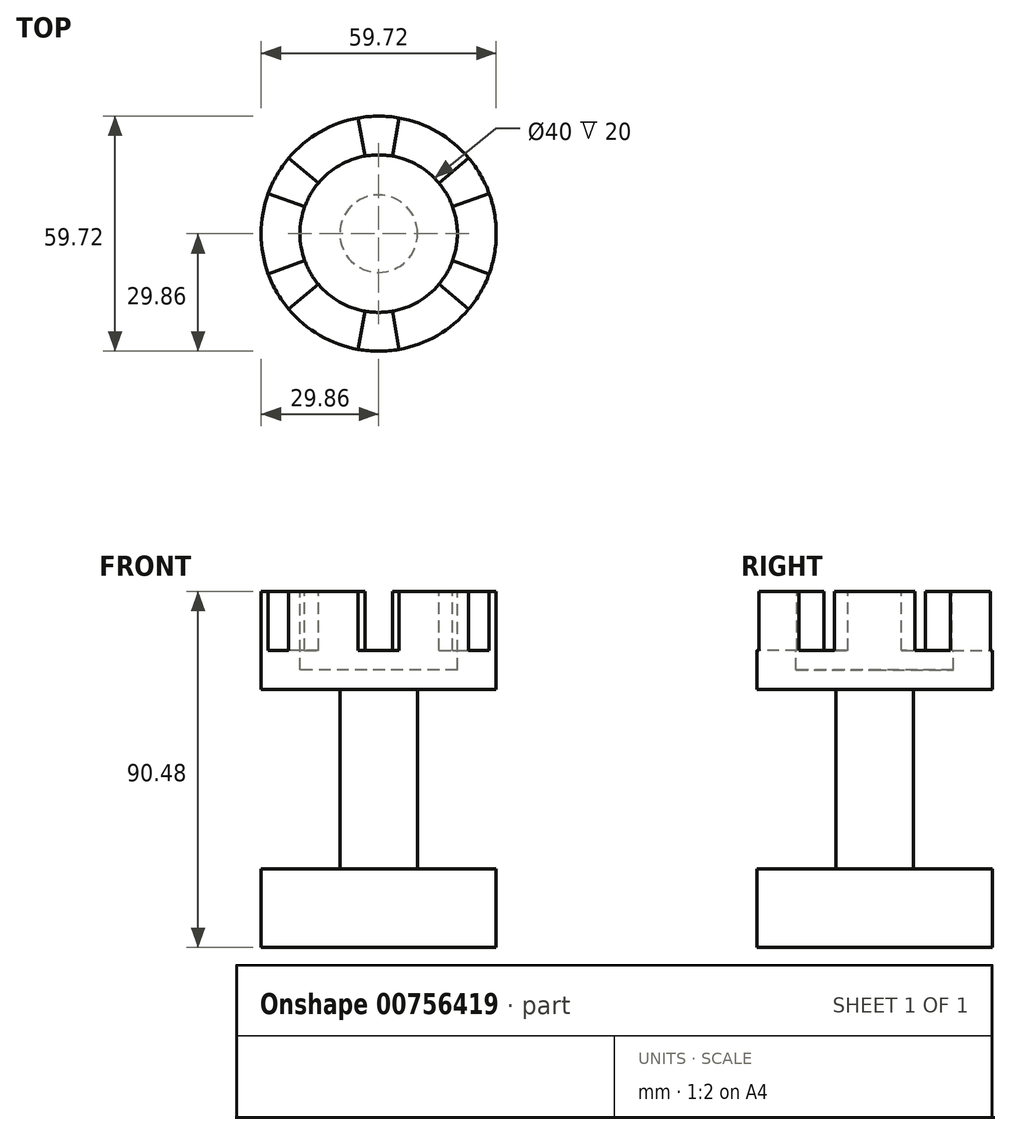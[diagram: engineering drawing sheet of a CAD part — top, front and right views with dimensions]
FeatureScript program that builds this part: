
annotation { "Feature Type Name" : "Feature", "Feature Type Description" : "" }
export const myFeature = defineFeature(function(context is Context, id is Id, definition is map)
    precondition{}
    {
        {
            var Q0;
            Q0=qCreatedBy(makeId("Front.planeOp"),FACE);
            var sketch = newSketch(context, id + "F0", { "sketchPlane" : qUnion([Q0])});
            skLineSegment(sketch, "E0.top", {"start": v(9.86, 20) * mm, "end": v(29.86, 20) * mm});
            skLineSegment(sketch, "E0.right", {"start": v(29.86, 0) * mm, "end": v(29.86, 20) * mm});
            skLineSegment(sketch, "E1.right", {"start": v(9.86, 20) * mm, "end": v(9.86, 65.48) * mm});
            skLineSegment(sketch, "E2.bottom", {"start": v(9.86, 65.48) * mm, "end": v(29.86, 65.48) * mm});
            skLineSegment(sketch, "E2.top", {"start": v(0, 90.48) * mm, "end": v(29.86, 90.48) * mm});
            skLineSegment(sketch, "E2.right", {"start": v(29.86, 65.48) * mm, "end": v(29.86, 90.48) * mm});
            skLineSegment(sketch, "E3", {"start": v(0, 90.48) * mm, "end": v(0, 0) * mm});
            skLineSegment(sketch, "E4", {"start": v(0, 0) * mm, "end": v(29.86, 0) * mm});
            skSolve(sketch);
        }
        {
            var Q0;
            Q0=qSketchRegion(id+"F0",true);
            var Q1;
            Q1=sQuery(id+"F0.wireOp",EDGE,"E3");
            revolve(context, id + "F1", {"surfaceOperationType" : NewSurfaceOperationType.NEW, "entities" : qUnion([Q0]), "axis" : qUnion([Q1]), "revolveType" : RevolveType.FULL});
        }
        {
            var Q0;
            Q0=makeQuery(id+"F1.opRevolve","SWEPT_FACE",FACE,{"disambiguationData":[OSD([sQuery(id+"F0.wireOp",EDGE,"E2.top")])]});
            var sketch = newSketch(context, id + "F2", { "sketchPlane" : qUnion([Q0])});
            skCircle(sketch, "E5", {"center": v(0, 0) * mm, "radius": 20 * mm});
            skSolve(sketch);
        }
        {
            var Q0;
            Q0 = qSketchRegion(id + "F2", true);
            extrude(context, id + "F3", {"entities" : qUnion([Q0]), "operationType" : NewBodyOperationType.REMOVE, "oppositeDirection" : true, "depth" : 20 * mm, "offsetDistance" : 25 * mm});
        }
        {
            var Q0;
            Q0=makeQuery(id+"F1.opRevolve","SWEPT_FACE",FACE,{"disambiguationData":[OSD([sQuery(id+"F0.wireOp",EDGE,"E2.top")])]});
            var sketch = newSketch(context, id + "F4", { "sketchPlane" : qUnion([Q0])});
            skLineSegment(sketch, "E6", {"start": v(3.01, 17.1) * mm, "end": v(6.24, 35.4) * mm});
            skLineSegment(sketch, "E7", {"start": v(-3.01, 17.1) * mm, "end": v(-6.24, 35.4) * mm});
            skArc(sketch, "E8", {"start": v(3.01, 17.1) * mm, "mid": v(0, 17.36) * mm, "end": v(-3.01, 17.1) * mm});
            skArc(sketch, "E9", {"start": v(6.24, 35.4) * mm, "mid": v(0, 35.94) * mm, "end": v(-6.24, 35.4) * mm});
            skLineSegment(sketch, "E10.1.0", {"start": v(-16.3, 5.94) * mm, "end": v(-33.78, 12.3) * mm});
            skArc(sketch, "E10.1.1", {"start": v(-27.53, 23.1) * mm, "mid": v(-31.13, 17.97) * mm, "end": v(-33.78, 12.3) * mm});
            skArc(sketch, "E10.1.2", {"start": v(-13.3, 11.16) * mm, "mid": v(-15.03, 8.68) * mm, "end": v(-16.3, 5.94) * mm});
            skLineSegment(sketch, "E10.1.3", {"start": v(-13.3, 11.16) * mm, "end": v(-27.53, 23.1) * mm});
            skLineSegment(sketch, "E10.2.0", {"start": v(-13.3, -11.16) * mm, "end": v(-27.53, -23.1) * mm});
            skArc(sketch, "E10.2.1", {"start": v(-33.78, -12.3) * mm, "mid": v(-31.13, -17.97) * mm, "end": v(-27.53, -23.1) * mm});
            skArc(sketch, "E10.2.2", {"start": v(-16.3, -5.94) * mm, "mid": v(-15.03, -8.68) * mm, "end": v(-13.3, -11.16) * mm});
            skLineSegment(sketch, "E10.2.3", {"start": v(-16.3, -5.94) * mm, "end": v(-33.78, -12.3) * mm});
            skLineSegment(sketch, "E10.3.0", {"start": v(3.01, -17.1) * mm, "end": v(6.24, -35.4) * mm});
            skArc(sketch, "E10.3.1", {"start": v(-6.24, -35.4) * mm, "mid": v(0, -35.94) * mm, "end": v(6.24, -35.4) * mm});
            skArc(sketch, "E10.3.2", {"start": v(-3.01, -17.1) * mm, "mid": v(0, -17.36) * mm, "end": v(3.01, -17.1) * mm});
            skLineSegment(sketch, "E10.3.3", {"start": v(-3.01, -17.1) * mm, "end": v(-6.24, -35.4) * mm});
            skLineSegment(sketch, "E10.4.0", {"start": v(16.3, -5.94) * mm, "end": v(33.78, -12.3) * mm});
            skArc(sketch, "E10.4.1", {"start": v(27.53, -23.1) * mm, "mid": v(31.13, -17.97) * mm, "end": v(33.78, -12.3) * mm});
            skArc(sketch, "E10.4.2", {"start": v(13.3, -11.16) * mm, "mid": v(15.03, -8.68) * mm, "end": v(16.3, -5.94) * mm});
            skLineSegment(sketch, "E10.4.3", {"start": v(13.3, -11.16) * mm, "end": v(27.53, -23.1) * mm});
            skLineSegment(sketch, "E10.5.0", {"start": v(13.3, 11.16) * mm, "end": v(27.53, 23.1) * mm});
            skArc(sketch, "E10.5.1", {"start": v(33.78, 12.3) * mm, "mid": v(31.13, 17.97) * mm, "end": v(27.53, 23.1) * mm});
            skArc(sketch, "E10.5.2", {"start": v(16.3, 5.94) * mm, "mid": v(15.03, 8.68) * mm, "end": v(13.3, 11.16) * mm});
            skLineSegment(sketch, "E10.5.3", {"start": v(16.3, 5.94) * mm, "end": v(33.78, 12.3) * mm});
            skSolve(sketch);
        }
        {
            var Q0;
            Q0 = qSketchRegion(id + "F4", true);
            extrude(context, id + "F5", {"entities" : qUnion([Q0]), "operationType" : NewBodyOperationType.REMOVE, "oppositeDirection" : true, "depth" : 15 * mm, "offsetDistance" : 25 * mm});
        }
    });
